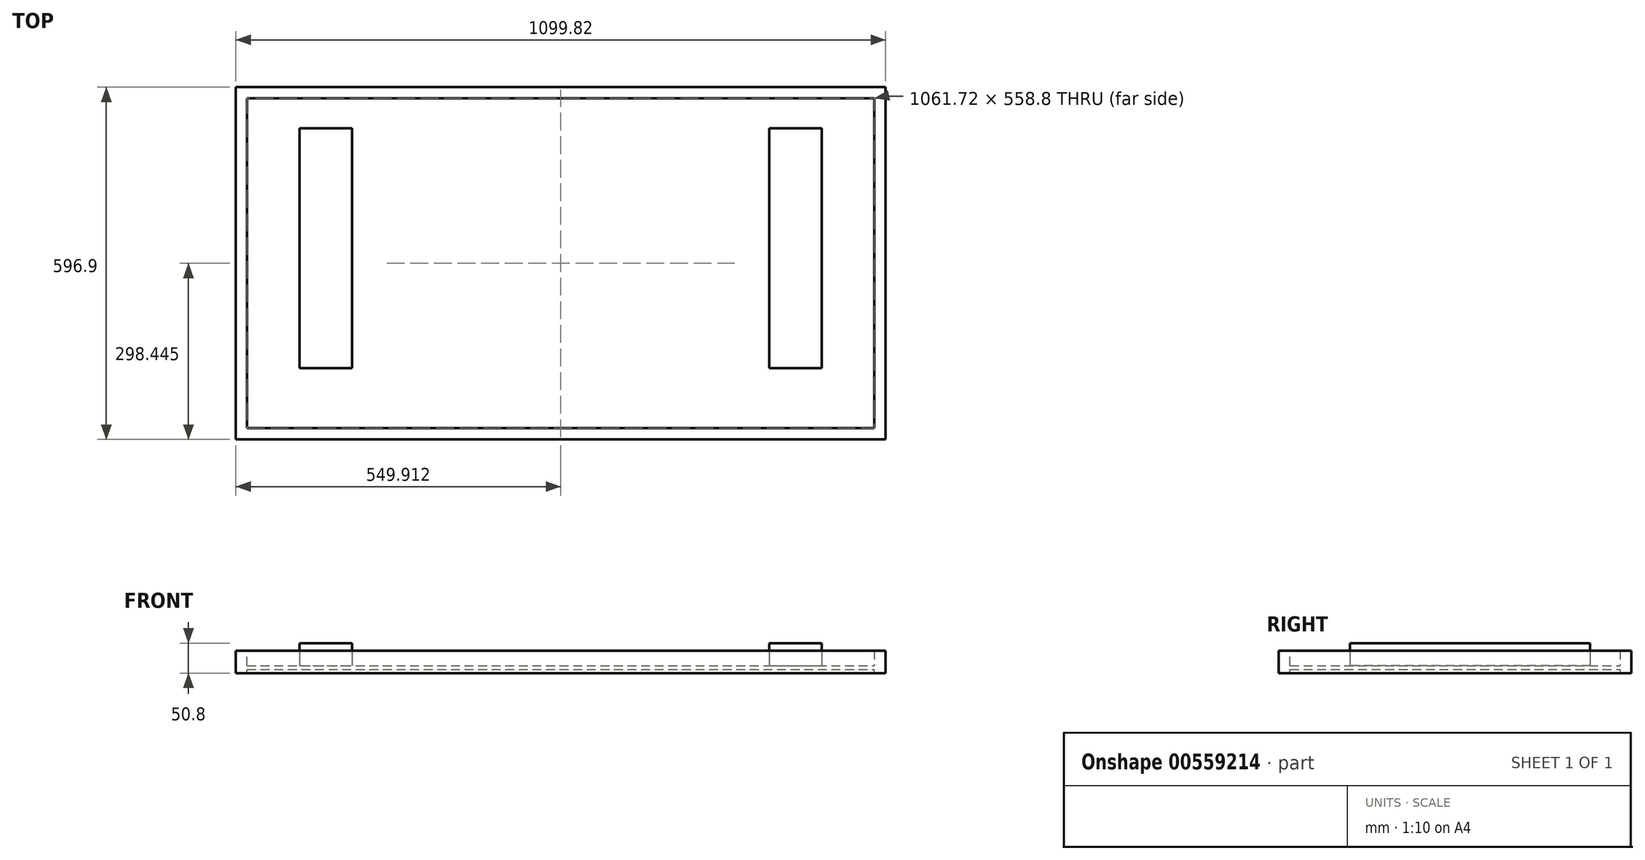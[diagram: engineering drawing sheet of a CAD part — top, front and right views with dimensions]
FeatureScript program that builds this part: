
annotation { "Feature Type Name" : "Feature", "Feature Type Description" : "" }
export const myFeature = defineFeature(function(context is Context, id is Id, definition is map)
    precondition{}
    {
        {
            var Q0;
            Q0=qCreatedBy(makeId("Top.planeOp"),FACE);
            var sketch = newSketch(context, id + "F0", { "sketchPlane" : qUnion([Q0])});
            skLineSegment(sketch, "E0.bottom", {"start": v(-54.43, -50.95) * mm, "end": v(1007.3, -50.95) * mm});
            skLineSegment(sketch, "E0.top", {"start": v(-54.43, 507.85) * mm, "end": v(1007.3, 507.85) * mm});
            skLineSegment(sketch, "E0.left", {"start": v(-54.43, -50.95) * mm, "end": v(-54.43, 507.85) * mm});
            skLineSegment(sketch, "E0.right", {"start": v(1007.3, -50.95) * mm, "end": v(1007.3, 507.85) * mm});
            skSolve(sketch);
        }
        {
            var Q0;
            Q0 = qSketchRegion(id + "F0", true);
            extrude(context, id + "F1", {"entities" : qUnion([Q0]), "depth" : 6.35 * mm, "offsetDistance" : 25.4 * mm});
        }
        {
            var Q0;
            Q0=makeQuery(id+"F1.opExtrude","SWEPT_FACE",FACE,{"disambiguationData":[OSD([sQuery(id+"F0.wireOp",EDGE,"E0.left")])]});
            var sketch = newSketch(context, id + "F2", { "sketchPlane" : qUnion([Q0])});
            skLineSegment(sketch, "E1.bottom", {"start": v(-526.9, -6.35) * mm, "end": v(-507.85, -6.35) * mm});
            skLineSegment(sketch, "E1.top", {"start": v(-526.9, 31.75) * mm, "end": v(-507.85, 31.75) * mm});
            skLineSegment(sketch, "E1.left", {"start": v(-526.9, -6.35) * mm, "end": v(-526.9, 31.75) * mm});
            skLineSegment(sketch, "E1.right", {"start": v(-507.85, -6.35) * mm, "end": v(-507.85, 31.75) * mm});
            skPoint(sketch, "E2.firstSnap0", {"position": v(-517.37, -6.35) * mm});
            skLineSegment(sketch, "E2.bottom", {"start": v(50.95, -6.35) * mm, "end": v(70, -6.35) * mm});
            skLineSegment(sketch, "E2.top", {"start": v(50.95, 31.75) * mm, "end": v(70, 31.75) * mm});
            skLineSegment(sketch, "E2.left", {"start": v(50.95, -6.35) * mm, "end": v(50.95, 31.75) * mm});
            skLineSegment(sketch, "E2.right", {"start": v(70, -6.35) * mm, "end": v(70, 31.75) * mm});
            skSolve(sketch);
        }
        {
            var Q0;
            Q0 = qSketchRegion(id + "F2", true);
            extrude(context, id + "F3", {"entities" : qUnion([Q0]), "oppositeDirection" : true, "depth" : 1080.77 * mm, "offsetDistance" : 25.4 * mm});
        }
        {
            var Q0;
            Q0=makeQuery(id+"F3.opExtrude","SWEPT_FACE",FACE,{"disambiguationData":[OSD([sQuery(id+"F2.wireOp",EDGE,"E1.left")])]});
            var sketch = newSketch(context, id + "F4", { "sketchPlane" : qUnion([Q0])});
            skLineSegment(sketch, "E3.bottom", {"start": v(-1026.34, 31.75) * mm, "end": v(-1007.3, 31.75) * mm});
            skLineSegment(sketch, "E3.top", {"start": v(-1026.34, -6.35) * mm, "end": v(-1007.3, -6.35) * mm});
            skLineSegment(sketch, "E3.left", {"start": v(-1026.34, 31.75) * mm, "end": v(-1026.34, -6.35) * mm});
            skLineSegment(sketch, "E3.right", {"start": v(-1007.3, 31.75) * mm, "end": v(-1007.3, -6.35) * mm});
            skLineSegment(sketch, "E4.bottom", {"start": v(54.43, 31.75) * mm, "end": v(73.48, 31.75) * mm});
            skLineSegment(sketch, "E4.top", {"start": v(54.43, -6.35) * mm, "end": v(73.48, -6.35) * mm});
            skLineSegment(sketch, "E4.left", {"start": v(54.43, 31.75) * mm, "end": v(54.43, -6.35) * mm});
            skLineSegment(sketch, "E4.right", {"start": v(73.48, 31.75) * mm, "end": v(73.48, -6.35) * mm});
            skSolve(sketch);
        }
        {
            var Q0;
            Q0 = qSketchRegion(id + "F4", true);
            extrude(context, id + "F5", {"entities" : qUnion([Q0]), "operationType" : NewBodyOperationType.ADD, "oppositeDirection" : true, "depth" : 596.9 * mm, "offsetDistance" : 25.4 * mm});
        }
        {
            var Q0;
            Q0=makeQuery(id+"F1.opExtrude","CAP_FACE",FACE,{"disambiguationData":[OSD([sQuery(id+"F0.wireOp",EDGE,"E0.bottom"),sQuery(id+"F0.wireOp",EDGE,"E0.top"),sQuery(id+"F0.wireOp",EDGE,"E0.left"),sQuery(id+"F0.wireOp",EDGE,"E0.right")])],"isStart":false});
            var sketch = newSketch(context, id + "F6", { "sketchPlane" : qUnion([Q0])});
            skLineSegment(sketch, "E5.bottom", {"start": v(34.47, 457.05) * mm, "end": v(123.37, 457.05) * mm});
            skLineSegment(sketch, "E5.top", {"start": v(34.47, 50.65) * mm, "end": v(123.37, 50.65) * mm});
            skLineSegment(sketch, "E5.left", {"start": v(34.47, 457.05) * mm, "end": v(34.47, 50.65) * mm});
            skLineSegment(sketch, "E5.right", {"start": v(123.37, 457.05) * mm, "end": v(123.37, 50.65) * mm});
            skLineSegment(sketch, "E6.bottom", {"start": v(829.5, 457.05) * mm, "end": v(918.4, 457.05) * mm});
            skLineSegment(sketch, "E6.top", {"start": v(829.5, 50.65) * mm, "end": v(918.4, 50.65) * mm});
            skLineSegment(sketch, "E6.left", {"start": v(829.5, 457.05) * mm, "end": v(829.5, 50.65) * mm});
            skLineSegment(sketch, "E6.right", {"start": v(918.4, 457.05) * mm, "end": v(918.4, 50.65) * mm});
            skSolve(sketch);
        }
        {
            var Q0;
            Q0 = qSketchRegion(id + "F6", true);
            extrude(context, id + "F7", {"entities" : qUnion([Q0]), "operationType" : NewBodyOperationType.ADD, "depth" : 38.1 * mm, "offsetDistance" : 25.4 * mm});
        }
    });
